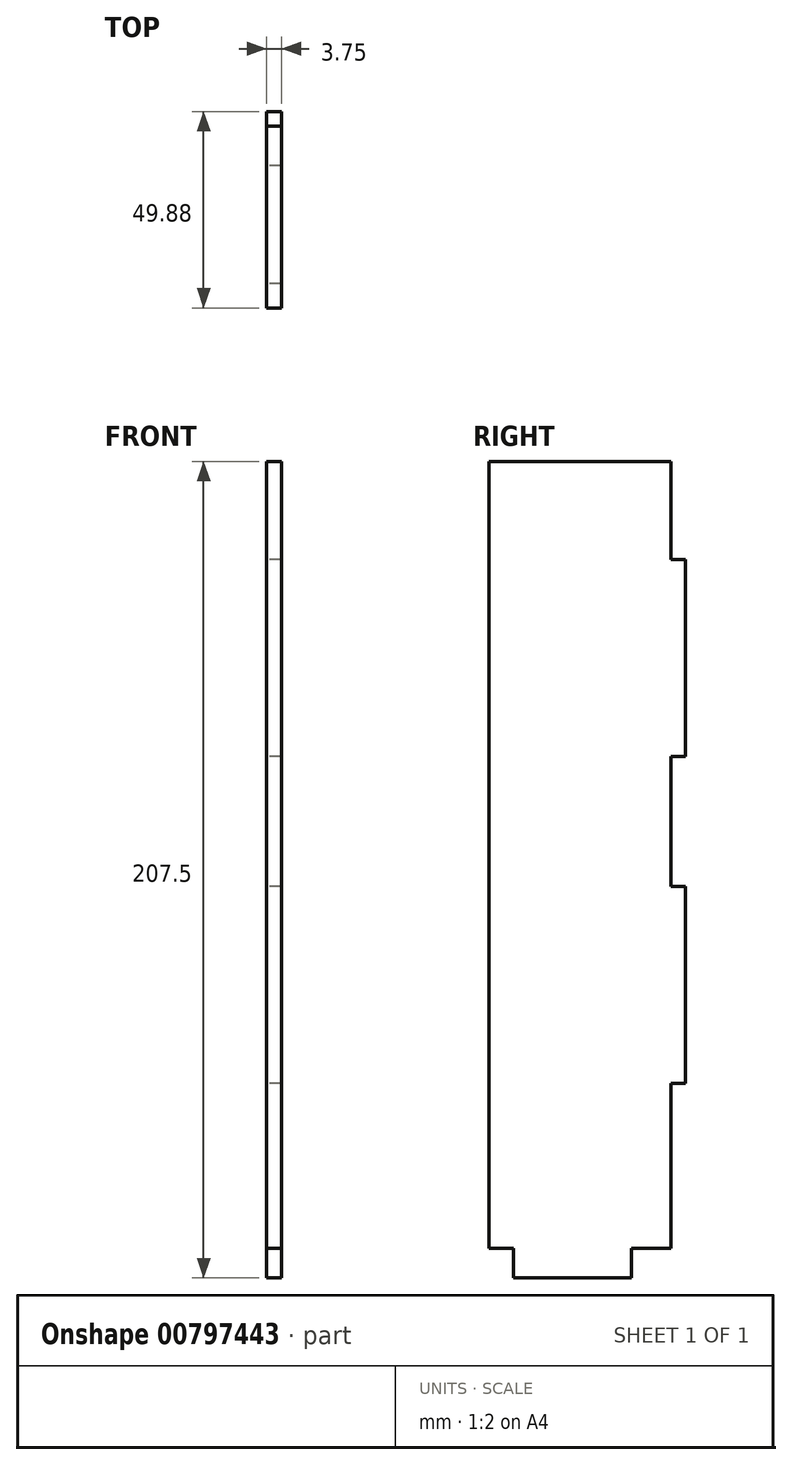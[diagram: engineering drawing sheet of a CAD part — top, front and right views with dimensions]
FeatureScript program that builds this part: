
annotation { "Feature Type Name" : "Feature", "Feature Type Description" : "" }
export const myFeature = defineFeature(function(context is Context, id is Id, definition is map)
    precondition{}
    {
        {
            var Q0;
            Q0=qCreatedBy(makeId("Right.planeOp"),FACE);
            var sketch = newSketch(context, id + "F0", { "sketchPlane" : qUnion([Q0])});
            skLineSegment(sketch, "E0.bottom", {"start": v(0, 8.05) * mm, "end": v(6.13, 8.05) * mm});
            skLineSegment(sketch, "E0.top", {"start": v(0, 208.05) * mm, "end": v(46.12, 208.05) * mm});
            skLineSegment(sketch, "E0.left", {"start": v(0, 8.05) * mm, "end": v(0, 208.05) * mm});
            skLineSegment(sketch, "E0.right", {"start": v(46.13, 8.05) * mm, "end": v(46.12, 50.05) * mm});
            skLineSegment(sketch, "E1.top", {"start": v(6.13, 0.55) * mm, "end": v(36.13, 0.55) * mm});
            skLineSegment(sketch, "E1.left", {"start": v(6.13, 8.05) * mm, "end": v(6.13, 0.55) * mm});
            skLineSegment(sketch, "E1.right", {"start": v(36.12, 8.05) * mm, "end": v(36.12, 0.55) * mm});
            skLineSegment(sketch, "E2", {"start": v(46.12, 8.05) * mm, "end": v(36.12, 8.05) * mm});
            skLineSegment(sketch, "E3.bottom", {"start": v(46.12, 183.05) * mm, "end": v(49.87, 183.05) * mm});
            skLineSegment(sketch, "E3.top", {"start": v(46.12, 133.05) * mm, "end": v(49.87, 133.05) * mm});
            skLineSegment(sketch, "E3.right", {"start": v(49.87, 183.05) * mm, "end": v(49.87, 133.05) * mm});
            skLineSegment(sketch, "E4.bottom", {"start": v(46.12, 100.05) * mm, "end": v(49.87, 100.05) * mm});
            skLineSegment(sketch, "E4.top", {"start": v(46.12, 50.05) * mm, "end": v(49.87, 50.05) * mm});
            skLineSegment(sketch, "E4.right", {"start": v(49.87, 100.05) * mm, "end": v(49.87, 50.05) * mm});
            skLineSegment(sketch, "E5.trimOffspring", {"start": v(46.12, 100.05) * mm, "end": v(46.12, 133.05) * mm});
            skLineSegment(sketch, "E6", {"start": v(46.12, 208.05) * mm, "end": v(46.12, 183.05) * mm});
            skSolve(sketch);
        }
        {
            var Q0;
            Q0=makeQuery(id+"F0.imprint","IMPRINT",FACE,{"disambiguationData":[TD([[makeQuery(id+"F0.imprint","IMPRINT",EDGE,{"derivedFrom":sQuery(id+"F0.wireOp",EDGE,"E0.bottom")}),1.0]])]});
            extrude(context, id + "F1", {"entities" : qUnion([Q0]), "depth" : 3.75 * mm, "offsetDistance" : 25 * mm});
        }
    });
